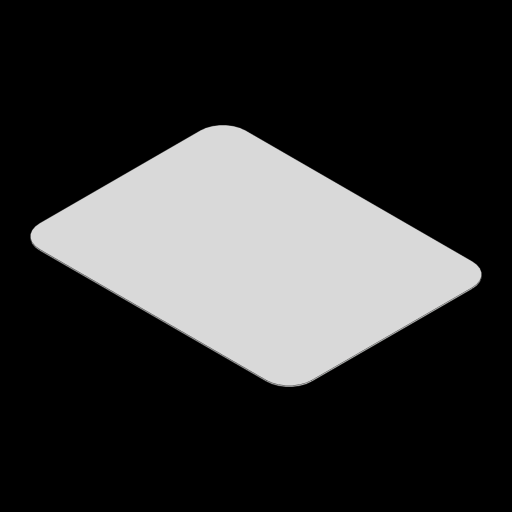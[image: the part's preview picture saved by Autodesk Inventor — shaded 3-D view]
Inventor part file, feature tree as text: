
AUTODESK INVENTOR PART (.ipt)
format: ipt  version: 2024 (Build 280153000, 153)  size: 93,184 bytes
history: native  units: mm
features: extrude x1, fillet x1, sketch x1
ambient origin geometry x8: Origin, YZ Plane, XZ Plane, XY Plane, X Axis, Y Axis, Z Axis, Center Point
bodies: Volumenkörper1 (feature_tree)
feature tree (3):
  extrude  "Extrusion1"  Depth=109.0mm
  fillet  "Rundung1"  Radius=0.6mm
  sketch  "Skizze1"  dims[d0=144.0mm d1=109.0mm d2=0.6mm d3=0.0mm d4=12.0mm]
